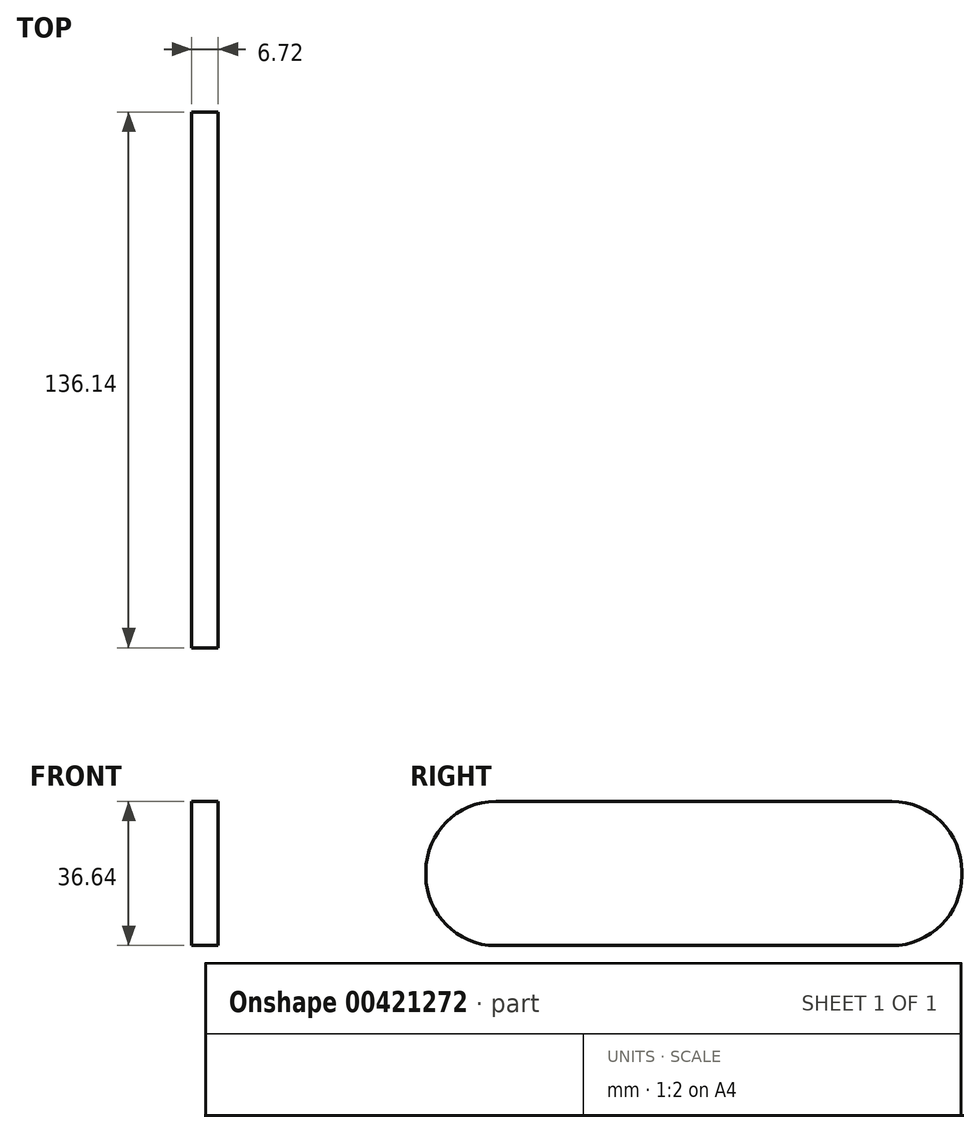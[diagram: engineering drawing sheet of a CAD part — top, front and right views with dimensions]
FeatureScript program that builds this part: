
annotation { "Feature Type Name" : "Feature", "Feature Type Description" : "" }
export const myFeature = defineFeature(function(context is Context, id is Id, definition is map)
    precondition{}
    {
        {
            var Q0;
            Q0=qCreatedBy(makeId("Front.planeOp"),FACE);
            var sketch = newSketch(context, id + "F0", { "sketchPlane" : qUnion([Q0])});
            skLineSegment(sketch, "E0.bottom", {"start": v(3.36, 18.32) * mm, "end": v(-3.36, 18.32) * mm});
            skLineSegment(sketch, "E0.top", {"start": v(3.36, -18.32) * mm, "end": v(-3.36, -18.32) * mm});
            skLineSegment(sketch, "E0.left", {"start": v(3.36, 18.32) * mm, "end": v(3.36, -18.32) * mm});
            skLineSegment(sketch, "E0.right", {"start": v(-3.36, 18.32) * mm, "end": v(-3.36, -18.32) * mm});
            skPoint(sketch, "E0.middle", {"position": v(0, 0) * mm});
            skSolve(sketch);
        }
        {
            var Q0;
            Q0=makeQuery(id+"F0.imprint","IMPRINT",FACE,{"disambiguationData":[TD([[makeQuery(id+"F0.imprint","IMPRINT",EDGE,{"derivedFrom":sQuery(id+"F0.wireOp",EDGE,"E0.bottom")}),1.0]])]});
            extrude(context, id + "F1", {"entities" : qUnion([Q0]), "depth" : 69.85 * mm, "offsetDistance" : 25.4 * mm, "hasSecondDirection" : true, "secondDirectionOppositeDirection" : true, "secondDirectionDepth" : 66.3 * mm});
        }
        {
            var Q0;
            Q0=makeQuery(id+"F1.opExtrude","CAP_EDGE",EDGE,{"disambiguationData":[OSD([sQuery(id+"F0.wireOp",EDGE,"E0.bottom")])],"isStart":false});
            fillet(context, id + "F2", {"entities" : qUnion([Q0]), "radius" : 17.78 * mm, "tangentPropagation" : true, "allowEdgeOverflow" : false});
        }
        {
            var Q0;
            Q0=makeQuery(id+"F1.opExtrude","CAP_EDGE",EDGE,{"disambiguationData":[OSD([sQuery(id+"F0.wireOp",EDGE,"E0.top")])],"isStart":false});
            fillet(context, id + "F3", {"entities" : qUnion([Q0]), "radius" : 17.78 * mm, "tangentPropagation" : true, "allowEdgeOverflow" : false});
        }
        {
            var Q0;
            Q0=makeQuery(id+"F1.opExtrude","CAP_EDGE",EDGE,{"disambiguationData":[OSD([sQuery(id+"F0.wireOp",EDGE,"E0.top")])],"isStart":true});
            var Q1;
            Q1=makeQuery(id+"F1.opExtrude","CAP_EDGE",EDGE,{"disambiguationData":[OSD([sQuery(id+"F0.wireOp",EDGE,"E0.bottom")])],"isStart":true});
            fillet(context, id + "F4", {"entities" : qUnion([Q0, Q1]), "radius" : 17.78 * mm, "tangentPropagation" : true, "allowEdgeOverflow" : false});
        }
    });
